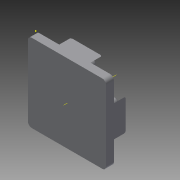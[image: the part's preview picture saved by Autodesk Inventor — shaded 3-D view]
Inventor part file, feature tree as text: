
AUTODESK INVENTOR PART (.ipt)
format: ipt  version: 2015 (Build 190159000, 159)  size: 179,200 bytes
history: native  units: mm
features: fillet x3, sketch x3, extrude x2, other x1, pattern_circular x1
ambient origin geometry x8: Origin, YZ Plane, XZ Plane, XY Plane, X Axis, Y Axis, Z Axis, Center Point
bodies: Solid1 (feature_tree)
feature tree (10):
  extrude  "Extrusion1"  Depth=20.0mm
  extrude  "Extrusion2"  Depth=4.0mm
  fillet  "Fillet1"  Radius=5.5mm
  fillet  "Fillet2"  Radius=1.8mm
  fillet  "Fillet3"  [1 undecoded]
  sketch  "Sketch3"  dims[d8=3.0mm d9=0.0mm d10=1.0mm d11=1.0mm d12=0.4mm d13=40.0mm d14=360.0deg]
  other  "Work Axis1"
  pattern_circular  "Circular Pattern1"  [2 undecoded]
  sketch  "Sketch1"  dims[d0=20.0mm d1=20.0mm]
  sketch  "Sketch2"  dims[d2=2.0mm d3=0.0mm d4=4.0mm d5=5.5mm d6=1.8mm d7=45.0deg]
note: 3 required parameter values undecoded (feature->parameter linkage not recoverable at this tier; creation-order binding heuristic only, values carry confidence <= 0.55)
